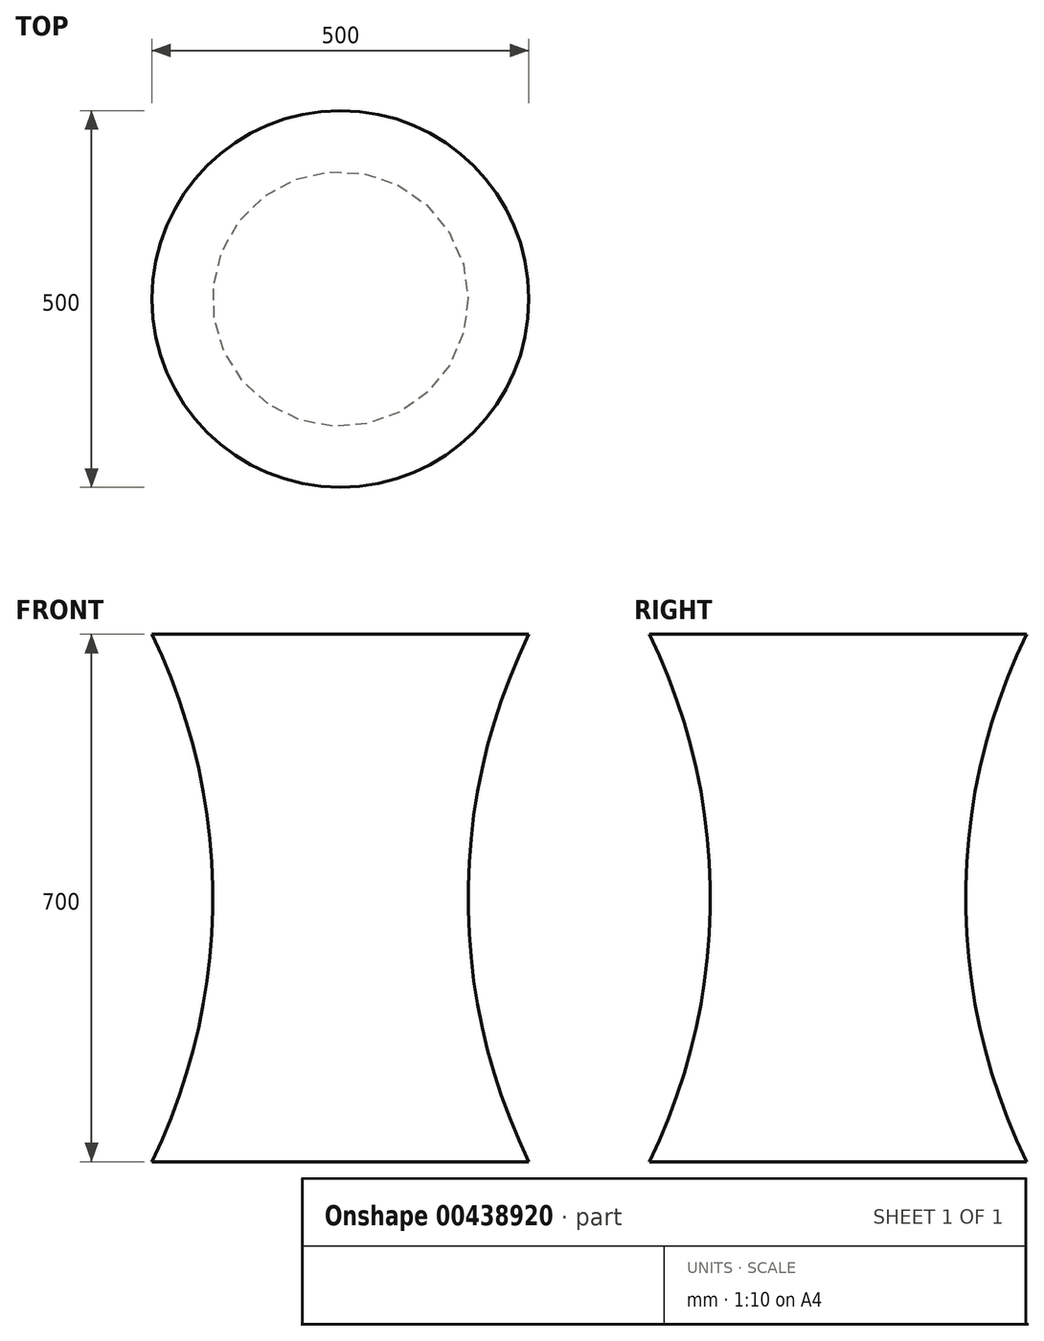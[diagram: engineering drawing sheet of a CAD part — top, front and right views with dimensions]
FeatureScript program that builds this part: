
annotation { "Feature Type Name" : "Feature", "Feature Type Description" : "" }
export const myFeature = defineFeature(function(context is Context, id is Id, definition is map)
    precondition{}
    {
        {
            var Q0;
            Q0=qCreatedBy(makeId("Front.planeOp"),FACE);
            var sketch = newSketch(context, id + "F0", { "sketchPlane" : qUnion([Q0])});
            skLineSegment(sketch, "E0", {"start": v(0, 279.77) * mm, "end": v(0, -299) * mm, "construction": true});
            skLineSegment(sketch, "E1", {"start": v(0, 0) * mm, "end": v(-250, 0) * mm});
            skArc(sketch, "E2", {"start": v(-250, 0) * mm, "mid": v(-169.37, 350) * mm, "end": v(-250, 700) * mm});
            skLineSegment(sketch, "E3", {"start": v(-250, 700) * mm, "end": v(0, 700) * mm});
            skLineSegment(sketch, "E4", {"start": v(0, 700) * mm, "end": v(0, 0) * mm});
            skSolve(sketch);
        }
        {
            var Q0;
            Q0 = qSketchRegion(id + "F0", true);
            var Q1;
            Q1=sQuery(id+"F0.wireOp",EDGE,"E0");
            revolve(context, id + "F1", {"entities" : qUnion([Q0]), "axis" : qUnion([Q1]), "revolveType" : RevolveType.FULL});
        }
    });
